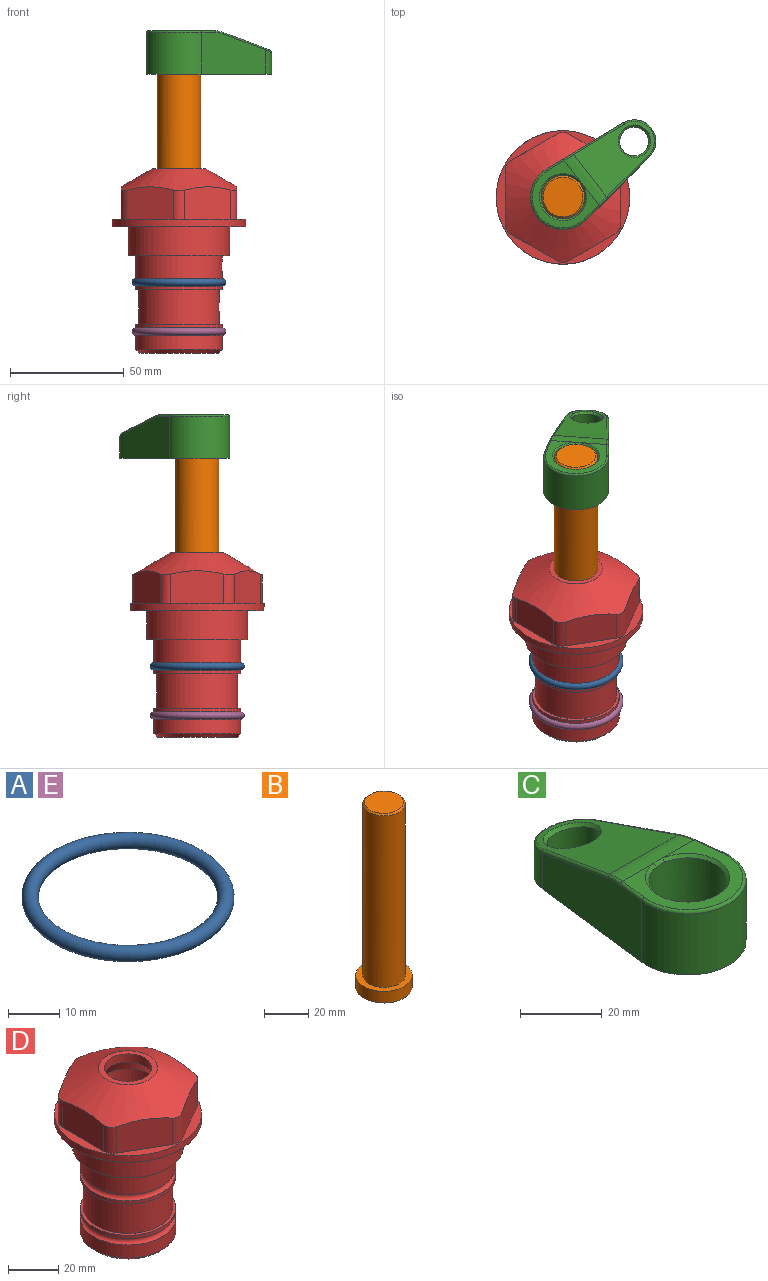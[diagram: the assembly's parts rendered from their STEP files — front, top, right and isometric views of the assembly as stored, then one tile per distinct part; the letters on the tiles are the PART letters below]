
ASSEMBLY  parts=5 mates=4
PART A: 1 faces, bbox 44.7x44.7x3.2 mm
  f0: torus R=19.05mm, axis (0,0,1), area 1193.9mm2
PART B: 6 faces, bbox 25.4x25.4x101.6 mm
  f0: plane 17.46x17.46mm, normal (0,0,1), area 239.5mm2, adj f5
  f1: plane 25.4x25.4mm, normal (0,0,-1), area 506.7mm2, adj f2
  f2: cylinder r=12.7mm len=25.4mm, axis (0,0,1), area 506.7mm2, adj f1,f3
  f3: plane 25.4x25.4mm, normal (0,0,1), area 221.7mm2, adj f2,f4
  f4: cylinder r=9.53mm len=94.46mm, axis (0,0,1), area 5653mm2, adj f3,f5
  f5: cone r=8.73mm half-angle=45deg, axis (0,0,-1), area 64.4mm2, adj f0,f4
PART C: 31 faces, bbox 31.7x65.5x19.8 mm
  f0: plane 39.12x18.26mm, normal (0.99,0.12,0), area 612.2mm2, adj f1,f4,f7,f11,f13,f15
  f1: cylinder r=9.53mm len=18.91mm, axis (0,0,-1), area 296.1mm2, adj f0,f2,f7,f17
  f2: plane 39.12x18.26mm, normal (-0.99,0.12,0), area 612.2mm2, adj f1,f4,f7,f12,f14,f16
  f3: cylinder r=6.35mm len=12.7mm, axis (0,0,-1), area 362.4mm2, adj f7,f18
  f4: cylinder r=14.29mm len=28.58mm, axis (0,0,-1), area 882.2mm2, adj f0,f2,f7,f10
  f5: cylinder r=9.53mm len=19.05mm, axis (0,0,-1), area 1092.6mm2, adj f7,f19,f20
  f6: plane 26.99x23.69mm, normal (0,0,1), area 216.2mm2, adj f9,f10,f11,f12,f19
  f7: plane 63.5x28.58mm, normal (0,0,-1), area 661.8mm2, adj f0,f1,f2,f3,f4,f5,f22,f23
  f8: plane 33.52x23.6mm, normal (0,0.26,0.97), area 486mm2, adj f9,f15,f16,f17,f18
  f9: cylinder r=19.05mm len=24.72mm, axis (1,0,0), area 120.4mm2, adj f6,f8,f13,f14,f20
  f10: torus R=13.49mm, axis (0,0,1), area 59mm2, adj f4,f6,f11,f12
  f11: cylinder r=0.79mm len=8.67mm, axis (0.12,-0.99,0), area 10.8mm2, adj f0,f6,f10,f13
  f12: cylinder r=0.79mm len=8.67mm, axis (0.12,0.99,0), area 10.8mm2, adj f2,f6,f10,f14
  f13: bspline ~4.95x1.42mm, area 6.1mm2, adj f0,f9,f11,f15
  f14: bspline ~4.95x1.42mm, area 6.1mm2, adj f2,f9,f12,f16
  f15: cylinder r=0.79mm len=25.95mm, axis (0.12,-0.96,0.26), area 32.9mm2, adj f0,f8,f13,f17
  f16: cylinder r=0.79mm len=25.95mm, axis (0.12,0.96,-0.26), area 32.9mm2, adj f2,f8,f14,f17
  f17: bspline ~18.91x8.38mm, area 30mm2, adj f1,f8,f15,f16
  f18: bspline ~14.29x14.29mm, area 48.3mm2, adj f3,f8
  f19: cone r=9.53mm half-angle=45deg, axis (0,0,1), area 66.5mm2, adj f5,f6,f20
  f20: bspline ~3.22x0.96mm, area 3.5mm2, adj f5,f9,f19
  f21: plane 2.75x2.72mm, normal (0,0,-1), area 2.9mm2, adj f23,f25,f28
  f22: plane 23.05x15.88mm, normal (-0.99,-0.12,0), area 323.6mm2, adj f7,f25,f26,f27,f28,f29
  f23: plane 23.05x15.88mm, normal (0.99,-0.12,0), area 323.6mm2, adj f7,f21,f25,f27,f28,f30
  f24: cylinder r=9.53mm len=10.69mm, axis (0,0,-1), area 114.7mm2, adj f7,f27,f29,f30
  f25: cylinder r=12.7mm len=20.59mm, axis (0,0,-1), area 381.1mm2, adj f7,f21,f22,f23,f26,f28
  f26: plane 2.75x2.72mm, normal (0,0,-1), area 2.9mm2, adj f22,f25,f28
  f27: plane 19.72x18.37mm, normal (0,-0.26,-0.97), area 291.8mm2, adj f22,f23,f24,f28,f29,f30
  f28: cylinder r=15.88mm len=19.92mm, axis (1,0,0), area 54.8mm2, adj f21,f22,f23,f25,f26,f27
  f29: cylinder r=1.59mm len=11mm, axis (0,0,-1), area 34.7mm2, adj f7,f22,f24,f27
  f30: cylinder r=1.59mm len=11mm, axis (0,0,-1), area 34.7mm2, adj f7,f23,f24,f27
PART D: 36 faces, bbox 58.7x58.7x81 mm
  f0: cylinder r=17.78mm len=35.56mm, axis (0,0,1), area 1670.8mm2, adj f23,f24,f31
  f1: cylinder r=19.05mm len=38.1mm, axis (0,0,1), area 1191.9mm2, adj f26,f27,f30
  f2: plane 58.66x58.66mm, normal (0,0,-1), area 1150.6mm2, adj f3,f28
  f3: cylinder r=29.33mm len=58.66mm, axis (0,0,-1), area 585.1mm2, adj f2,f4
  f4: plane 58.66x58.66mm, normal (0,0,1), area 475.9mm2, adj f3,f5,f6,f7,f8,f9,f10,f11
  f5: plane 20.32x14.34mm, normal (-0.5,0.87,0), area 324.4mm2, adj f4,f15,f16,f17
  f6: plane 20.32x14.34mm, normal (0.5,0.87,0), area 324.4mm2, adj f4,f14,f15,f17
  f7: plane 23.48x14.34mm, normal (1,0,0), area 324.4mm2, adj f4,f13,f14,f17
  f8: plane 20.32x14.34mm, normal (0.5,-0.87,0), area 324.4mm2, adj f4,f12,f13,f17
  f9: plane 20.32x14.34mm, normal (-0.5,-0.87,0), area 324.4mm2, adj f4,f11,f12,f17
  f10: plane 23.48x14.34mm, normal (-1,0,0), area 324.4mm2, adj f4,f11,f16,f17
  f11: cylinder r=5.08mm len=12.85mm, axis (0,0,-1), area 67.2mm2, adj f4,f9,f10,f17
  f12: cylinder r=5.08mm len=12.85mm, axis (0,0,-1), area 67.2mm2, adj f4,f8,f9,f17
  f13: cylinder r=5.08mm len=12.85mm, axis (0,0,-1), area 67.2mm2, adj f4,f7,f8,f17
  f14: cylinder r=5.08mm len=12.85mm, axis (0,0,-1), area 67.2mm2, adj f4,f6,f7,f17
  f15: cylinder r=5.08mm len=12.85mm, axis (0,0,-1), area 67.2mm2, adj f4,f5,f6,f17
  f16: cylinder r=5.08mm len=12.85mm, axis (0,0,-1), area 67.2mm2, adj f4,f5,f10,f17
  f17: cone r=11.73mm half-angle=60deg, axis (0,0,-1), area 2071.8mm2, adj f5,f6,f7,f8,f9,f10,f11,f12
  f18: plane 23.46x23.46mm, normal (0,0,1), area 147.4mm2, adj f17,f35
  f19: plane 34.93x34.93mm, normal (0,0,-1), area 958mm2, adj f29
  f20: cylinder r=19.05mm len=38.1mm, axis (0,0,1), area 760.1mm2, adj f21,f29
  f21: torus R=19.05mm, axis (0,0,1), area 565.3mm2, adj f20,f22
  f22: cylinder r=19.05mm len=38.1mm, axis (0,0,1), area 190mm2, adj f21,f23
  f23: plane 38.1x38.1mm, normal (0,0,1), area 146.9mm2, adj f0,f22
  f24: plane 38.1x38.1mm, normal (0,0,-1), area 146.9mm2, adj f0,f25
  f25: cylinder r=19.05mm len=38.1mm, axis (0,0,1), area 190mm2, adj f24,f26
  f26: torus R=19.05mm, axis (0,0,1), area 565.3mm2, adj f1,f25
  f27: plane 44.45x44.45mm, normal (0,0,-1), area 411.7mm2, adj f1,f28
  f28: cylinder r=22.23mm len=44.45mm, axis (0,0,1), area 1773.5mm2, adj f2,f27
  f29: cone r=19.05mm half-angle=45deg, axis (0,0,1), area 257.5mm2, adj f19,f20
  f30: cylinder r=3.17mm len=6.75mm, axis (-1,0,0), area 128mm2, adj f1,f33
  f31: cylinder r=3.17mm len=6.35mm, axis (-1,0,0), area 102.5mm2, adj f0,f33
  f32: plane 25.4x25.4mm, normal (0,0,1), area 506.7mm2, adj f33
  f33: cylinder r=12.7mm len=66.42mm, axis (0,0,-1), area 5236.2mm2, adj f30,f31,f32,f34
  f34: cone r=9.53mm half-angle=30deg, axis (0,0,-1), area 443.4mm2, adj f33,f35
  f35: cylinder r=9.53mm len=19.05mm, axis (0,0,-1), area 240.9mm2, adj f18,f34
PART E: same geometry as A
PLACE A at identity
PLACE B rot(axis=(0,0,-1),52deg) t=(0,0,22.52)mm
PLACE C rot(axis=(0,0,-1),52deg) t=(0,0,22.52)mm
PLACE D at identity fixed
PLACE E t=(0,0,-21.59)mm
MATE fastened E.f0 <-> D.f0  axis (0,0,1) through (0,0,-46.1)mm
MATE fastened A.f0 <-> D.f0  axis (0,0,1) through (0,0,-24.51)mm
MATE fastened B.f2 <-> C.f4  axis (0,0,1) through (0,0,86.02)mm
MATE cylindrical B.f2 <-> D.f0  axis (0,0,-1) through (0,0,-15.58)mm
